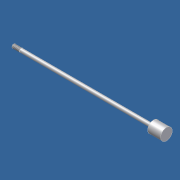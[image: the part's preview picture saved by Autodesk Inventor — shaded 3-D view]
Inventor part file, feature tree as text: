
AUTODESK INVENTOR PART (.ipt)
format: ipt  version: 2012 (Build 160160000, 160)  size: 124,416 bytes
history: native  units: in
note: dims shown in document units (in); Inventor stores cm internally (conversion verified against a paired STEP export)
features: other x84, revolve x3, sketch x3, thread x1
ambient origin geometry x8: Origin, YZ Plane, XZ Plane, XY Plane, X Axis, Y Axis, Z Axis, Center Point
bodies: Solid1 (feature_tree)
feature tree (91):
  revolve  "Revolution1"  Angle=360.0deg
  revolve  "Revolution2"  Angle=360.0deg
  thread  "Thread1"  [1 undecoded]
  revolve  "Revolution3"  [1 undecoded]
  other  "rod_cp_XY"
  other  "rod_cp_YZ"
  other  "rod_cp_ZX"
  other  "rod_cp_X"
  other  "rod_cp_Y"
  other  "rod_cp_Z"
  other  "rod_cp_Center"
  other  "to_rod_clevis_XY"
  other  "to_rod_clevis_YZ"
  other  "to_rod_clevis_ZX"
  other  "to_rod_clevis_X"
  other  "to_rod_clevis_Y"
  other  "to_rod_clevis_Z"
  other  "to_rod_clevis_Center"
  other  "rl2_XY"
  other  "rl2_YZ"
  other  "rl2_ZX"
  other  "rl2_X"
  other  "rl2_Y"
  other  "rl2_Z"
  other  "rl2_Center"
  other  "rl1_XY"
  other  "rl1_YZ"
  other  "rl1_ZX"
  other  "rl1_X"
  other  "rl1_Y"
  other  "rl1_Z"
  other  "rl1_Center"
  other  "thd1_XY"
  other  "thd1_YZ"
  other  "thd1_ZX"
  other  "thd1_X"
  other  "thd1_Y"
  other  "thd1_Z"
  other  "thd1_Center"
  other  "thd2_XY"
  other  "thd2_YZ"
  other  "thd2_ZX"
  other  "thd2_X"
  other  "thd2_Y"
  other  "thd2_Z"
  other  "thd2_Center"
  other  "dia1_XY"
  other  "dia1_YZ"
  other  "dia1_ZX"
  other  "dia1_X"
  other  "dia1_Y"
  other  "dia1_Z"
  other  "dia1_Center"
  other  "dia2_XY"
  other  "dia2_YZ"
  other  "dia2_ZX"
  other  "dia2_X"
  other  "dia2_Y"
  other  "dia2_Z"
  other  "dia2_Center"
  other  "hh1_XY"
  other  "hh1_YZ"
  other  "hh1_ZX"
  other  "hh1_X"
  other  "hh1_Y"
  other  "hh1_Z"
  other  "hh1_Center"
  other  "hh2_XY"
  other  "hh2_YZ"
  other  "hh2_ZX"
  other  "hh2_X"
  other  "hh2_Y"
  other  "hh2_Z"
  other  "hh2_Center"
  other  "dia12_XY"
  other  "dia12_YZ"
  other  "dia12_ZX"
  other  "dia12_X"
  other  "dia12_Y"
  other  "dia12_Z"
  other  "dia12_Center"
  other  "dia22_XY"
  other  "dia22_YZ"
  other  "dia22_ZX"
  other  "dia22_X"
  other  "dia22_Y"
  other  "dia22_Z"
  other  "dia22_Center"
  sketch  "Sketch_1"  dims[d0=360.0deg d1=360.0deg]
  sketch  "Sketch_3"  dims[d2=0.5in d3=8.594in d4=360.0deg]
  sketch  "Sketch_30"
note: 2 required parameter values undecoded (feature->parameter linkage not recoverable at this tier; creation-order binding heuristic only, values carry confidence <= 0.55)
